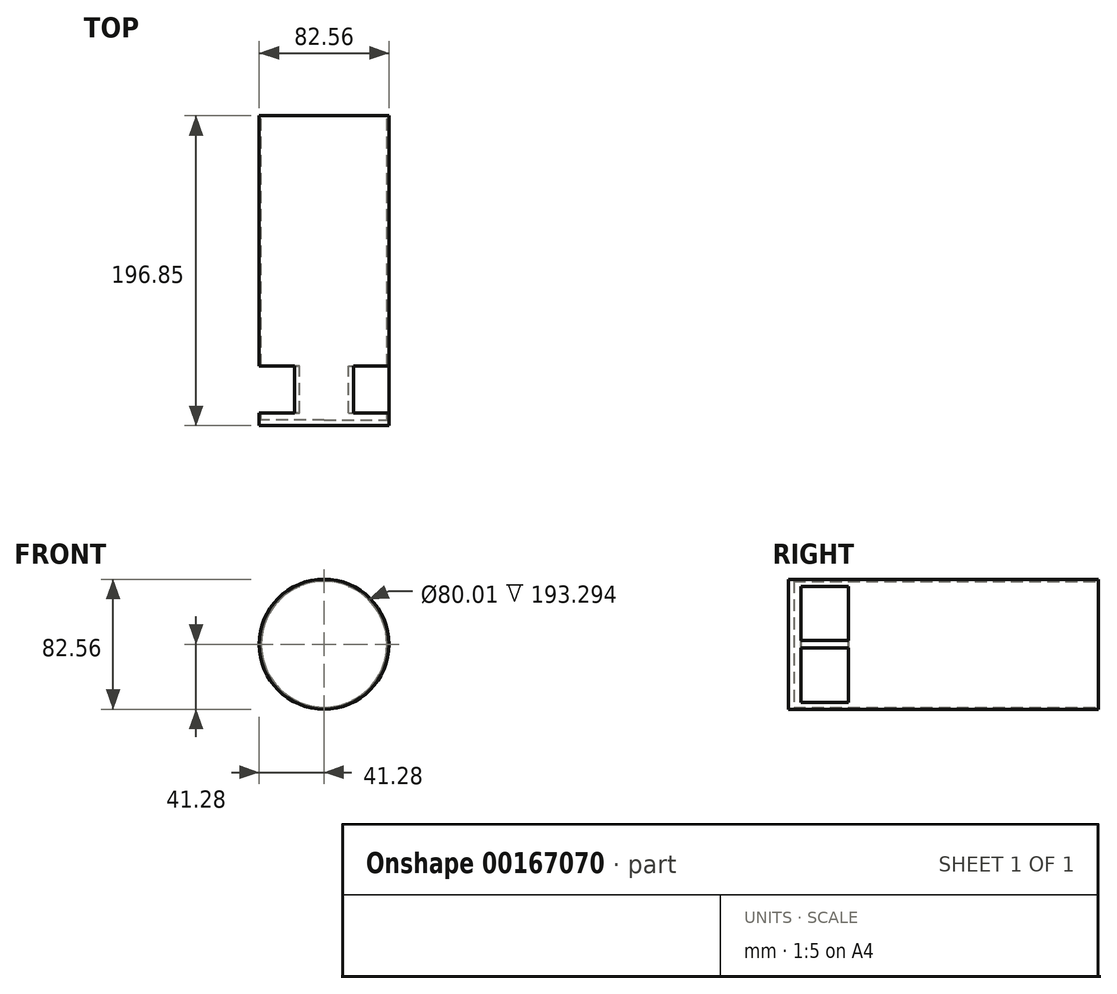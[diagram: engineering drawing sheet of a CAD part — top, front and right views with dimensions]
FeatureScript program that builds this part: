
annotation { "Feature Type Name" : "Feature", "Feature Type Description" : "" }
export const myFeature = defineFeature(function(context is Context, id is Id, definition is map)
    precondition{}
    {
        {
            var Q0;
            Q0=qCreatedBy(makeId("Front.planeOp"),FACE);
            var sketch = newSketch(context, id + "F0", { "sketchPlane" : qUnion([Q0])});
            skCircle(sketch, "E0", {"center": v(0, 0) * mm, "radius": 41.28 * mm});
            skSolve(sketch);
        }
        {
            var Q0;
            Q0 = qSketchRegion(id + "F0", true);
            extrude(context, id + "F1", {"entities" : qUnion([Q0]), "endBound" : BoundingType.SYMMETRIC, "depth" : 203.2 * mm});
        }
        {
            var Q0;
            Q0=qCreatedBy(makeId("Top.planeOp"),FACE);
            var sketch = newSketch(context, id + "F2", { "sketchPlane" : qUnion([Q0])});
            skLineSegment(sketch, "E1.bottom", {"start": v(-41.54, -93.43) * mm, "end": v(41.21, -93.43) * mm});
            skLineSegment(sketch, "E1.top", {"start": v(-41.54, -63.53) * mm, "end": v(41.21, -63.53) * mm});
            skLineSegment(sketch, "E1.left", {"start": v(-41.54, -93.43) * mm, "end": v(-41.54, -63.53) * mm});
            skLineSegment(sketch, "E1.right", {"start": v(41.21, -93.43) * mm, "end": v(41.21, -63.53) * mm});
            skSolve(sketch);
        }
        {
            var Q0;
            Q0 = qSketchRegion(id + "F2", true);
            extrude(context, id + "F3", {"entities" : qUnion([Q0]), "operationType" : NewBodyOperationType.REMOVE, "endBound" : BoundingType.SYMMETRIC, "oppositeDirection" : true, "depth" : 73.66 * mm});
        }
        {
            var Q0;
            Q0=qCreatedBy(makeId("Front.planeOp"),FACE);
            var sketch = newSketch(context, id + "F4", { "sketchPlane" : qUnion([Q0])});
            skCircle(sketch, "E2", {"center": v(0, 0) * mm, "radius": 40 * mm});
            skSolve(sketch);
        }
        {
            var Q0;
            Q0 = qSketchRegion(id + "F4", true);
            extrude(context, id + "F5", {"entities" : qUnion([Q0]), "operationType" : NewBodyOperationType.REMOVE, "endBound" : BoundingType.SYMMETRIC, "depth" : 196.1 * mm});
        }
        {
            var Q0;
            Q0=makeQuery(id+"F1.opExtrude","CAP_FACE",FACE,{"disambiguationData":[OSD([sQuery(id+"F0.wireOp",EDGE,"E0")])],"isStart":true});
            var sketch = newSketch(context, id + "F6", { "sketchPlane" : qUnion([Q0])});
            skCircle(sketch, "E3.1", {"center": v(0, 0) * mm, "radius": 41.28 * mm});
            skSolve(sketch);
        }
        {
            var Q0;
            Q0 = qSketchRegion(id + "F6", true);
            extrude(context, id + "F7", {"entities" : qUnion([Q0]), "operationType" : NewBodyOperationType.REMOVE, "endBound" : BoundingType.SYMMETRIC, "oppositeDirection" : true, "depth" : 12.7 * mm});
        }
    });
